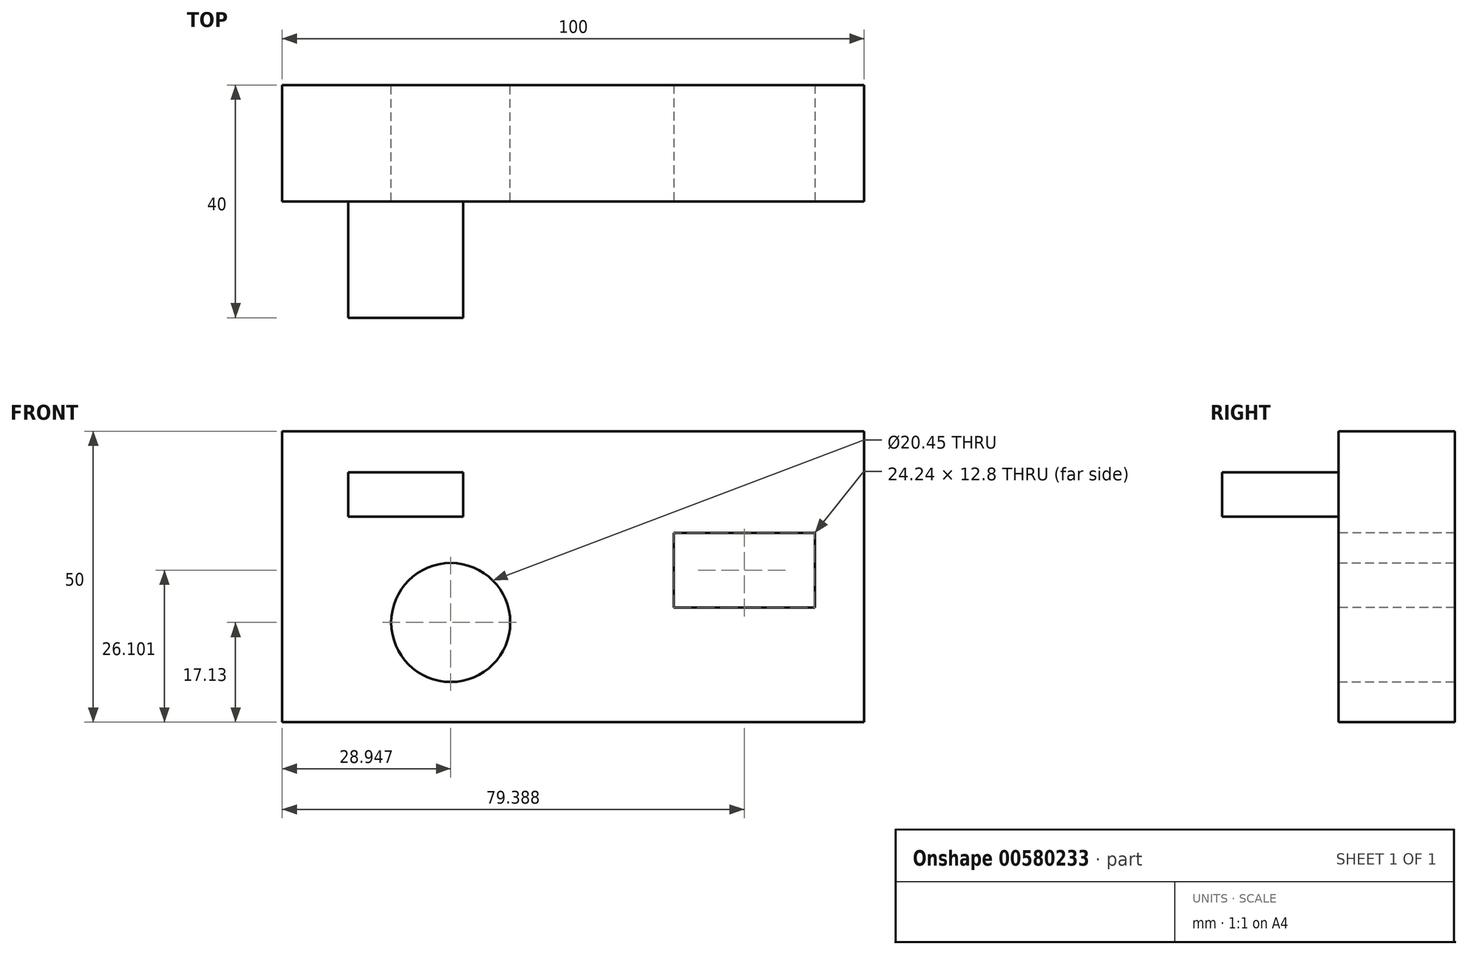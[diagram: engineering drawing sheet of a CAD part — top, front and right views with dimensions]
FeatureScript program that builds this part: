
annotation { "Feature Type Name" : "Feature", "Feature Type Description" : "" }
export const myFeature = defineFeature(function(context is Context, id is Id, definition is map)
    precondition{}
    {
        {
            var Q0;
            Q0=qCreatedBy(makeId("Front.planeOp"),FACE);
            var sketch = newSketch(context, id + "F0", { "sketchPlane" : qUnion([Q0])});
            skLineSegment(sketch, "E0.bottom", {"start": v(0, 0) * mm, "end": v(100, 0) * mm});
            skLineSegment(sketch, "E0.top", {"start": v(0, 50) * mm, "end": v(100, 50) * mm});
            skLineSegment(sketch, "E0.left", {"start": v(0, 0) * mm, "end": v(0, 50) * mm});
            skLineSegment(sketch, "E0.right", {"start": v(100, 0) * mm, "end": v(100, 50) * mm});
            skSolve(sketch);
        }
        {
            var Q0;
            Q0=makeQuery(id+"F0.imprint","IMPRINT",FACE,{"disambiguationData":[TD([[makeQuery(id+"F0.imprint","IMPRINT",EDGE,{"derivedFrom":sQuery(id+"F0.wireOp",EDGE,"E0.bottom")}),1.0]])]});
            extrude(context, id + "F1", {"entities" : qUnion([Q0]), "depth" : 20 * mm, "offsetDistance" : 25.4 * mm});
        }
        {
            var Q0;
            Q0=qCreatedBy(makeId("Front.planeOp"),FACE);
            var sketch = newSketch(context, id + "F2", { "sketchPlane" : qUnion([Q0])});
            skCircle(sketch, "E1", {"center": v(28.95, 17.13) * mm, "radius": 10.23 * mm});
            skSolve(sketch);
        }
        {
            var Q0;
            Q0 = qSketchRegion(id + "F2", true);
            extrude(context, id + "F3", {"entities" : qUnion([Q0]), "operationType" : NewBodyOperationType.REMOVE, "endBound" : BoundingType.THROUGH_ALL, "depth" : 76.2 * mm, "offsetDistance" : 25.4 * mm});
        }
        {
            var Q0;
            Q0=makeQuery(id+"F1.opExtrude","CAP_FACE",FACE,{"disambiguationData":[OSD([sQuery(id+"F0.wireOp",EDGE,"E0.bottom"),sQuery(id+"F0.wireOp",EDGE,"E0.top"),sQuery(id+"F0.wireOp",EDGE,"E0.left"),sQuery(id+"F0.wireOp",EDGE,"E0.right")])],"isStart":false});
            var sketch = newSketch(context, id + "F4", { "sketchPlane" : qUnion([Q0])});
            skLineSegment(sketch, "E2.bottom", {"start": v(67.27, 32.5) * mm, "end": v(91.5, 32.5) * mm});
            skLineSegment(sketch, "E2.top", {"start": v(67.27, 19.7) * mm, "end": v(91.5, 19.7) * mm});
            skLineSegment(sketch, "E2.left", {"start": v(67.27, 32.5) * mm, "end": v(67.27, 19.7) * mm});
            skLineSegment(sketch, "E2.right", {"start": v(91.5, 32.5) * mm, "end": v(91.5, 19.7) * mm});
            skSolve(sketch);
        }
        {
            var Q0;
            Q0=makeQuery(id+"F4.imprint","IMPRINT",FACE,{"disambiguationData":[TD([[makeQuery(id+"F4.imprint","IMPRINT",EDGE,{"derivedFrom":sQuery(id+"F4.wireOp",EDGE,"E2.bottom")}),-1.0]])]});
            extrude(context, id + "F5", {"entities" : qUnion([Q0]), "operationType" : NewBodyOperationType.REMOVE, "endBound" : BoundingType.THROUGH_ALL, "oppositeDirection" : true, "depth" : 25.4 * mm, "offsetDistance" : 25.4 * mm});
        }
        {
            var Q0;
            Q0=makeQuery(id+"F4.imprint","IMPRINT",FACE,{"disambiguationData":[TD([[makeQuery(id+"F4.imprint","IMPRINT",EDGE,{"derivedFrom":sQuery(id+"F4.wireOp",EDGE,"E2.bottom")}),1.0]])]});
            var sketch = newSketch(context, id + "F6", { "sketchPlane" : qUnion([Q0])});
            skLineSegment(sketch, "E3.bottom", {"start": v(11.36, 42.93) * mm, "end": v(31.09, 42.93) * mm});
            skLineSegment(sketch, "E3.top", {"start": v(11.36, 35.34) * mm, "end": v(31.09, 35.34) * mm});
            skLineSegment(sketch, "E3.left", {"start": v(11.36, 42.93) * mm, "end": v(11.36, 35.34) * mm});
            skLineSegment(sketch, "E3.right", {"start": v(31.09, 42.93) * mm, "end": v(31.09, 35.34) * mm});
            skSolve(sketch);
        }
        {
            var Q0;
            Q0=makeQuery(id+"F6.imprint","IMPRINT",FACE,{"disambiguationData":[TD([[makeQuery(id+"F6.imprint","IMPRINT",EDGE,{"derivedFrom":sQuery(id+"F6.wireOp",EDGE,"E3.bottom")}),-1.0]])]});
            extrude(context, id + "F7", {"entities" : qUnion([Q0]), "operationType" : NewBodyOperationType.ADD, "depth" : 20 * mm, "offsetDistance" : 25.4 * mm});
        }
    });
